# Revit family: Bath-Freestanding-BubbleMassage-Air_Bath-Heated_Surface-KOHLER-COMFORTABLE-K-99779T_1
name_source: partatom
category: Plumbing Fixtures
revit_build: Autodesk Revit 2017 (Build: 20160225_1515(x64)
units: mm (PartAtom-declared; Revit-internal decimal feet)

## family parameters
Cut with Voids When Loaded = No
Host = Face
OmniClass Number = 23.31.15.00
OmniClass Title = Bathtubs
Part Type = Normal
Room Calculation Point = No
Round Connector Dimension = Use Diameter
Shared = No

## types (2) — shared parameters
ADA Compliant = No
Amplifer Electrical Connector = Amplifer Electrical Connector
Apparent Load = 0 VA
Assembly Code = D2010500
Blower Electrical Connector = Blower Electrical Connector
CW Connection = No
Cold Water Inlet = Cold Water Inlet
Date Modified = 01/29/2021
Default Elevation = 0"
Description = COMFORTABLE BBM 1.7M FS W/ GR & MSG PL
Drain Included = No
Electrical Connector = Yes
Electrical Note = Two dedicate circuit required
Finish = KOHLER-Acrylic-0-White
HW Connection = No
Heater Electrical Connector = Heater Electrical Connector
Height = 28 7/16"
Hot Water Inlet = Hot Water Inlet
Length = 66 15/16"
Manufacturer = KOHLER Co.
Master Format 2014 = 22 41 19
Master Format 2014 Name = Residential Bathtubs
Material = Acrylic
Product Documentation Link = https://files.kohler.com.cn
Product Name = COMFORTABLE
Product Page URL = https://www.kohler.com.cn
Pump Electrical Connector = Pump Electrical Connector
URL = http://www.kohler.com.cn
Vent Connection = No
Voltage = 240 V
Waste Connection = Yes
Waste Water Outlet = Waste Water Outlet
WaterSense Certified = No
Width = 31 7/16"

## per-type parameters (varying)
| type | G58 | GGR58 | Model | Type |
| G58, 0-White | Yes | No | K-99779T-G58-0 | 1 |
| GGR58, 0-White | No | Yes | K-99779T-GGR58-0 | 2 |

## geometry (parser evidence)
native form markers: Sweep x4
no freeform markers — native parametric forms only
